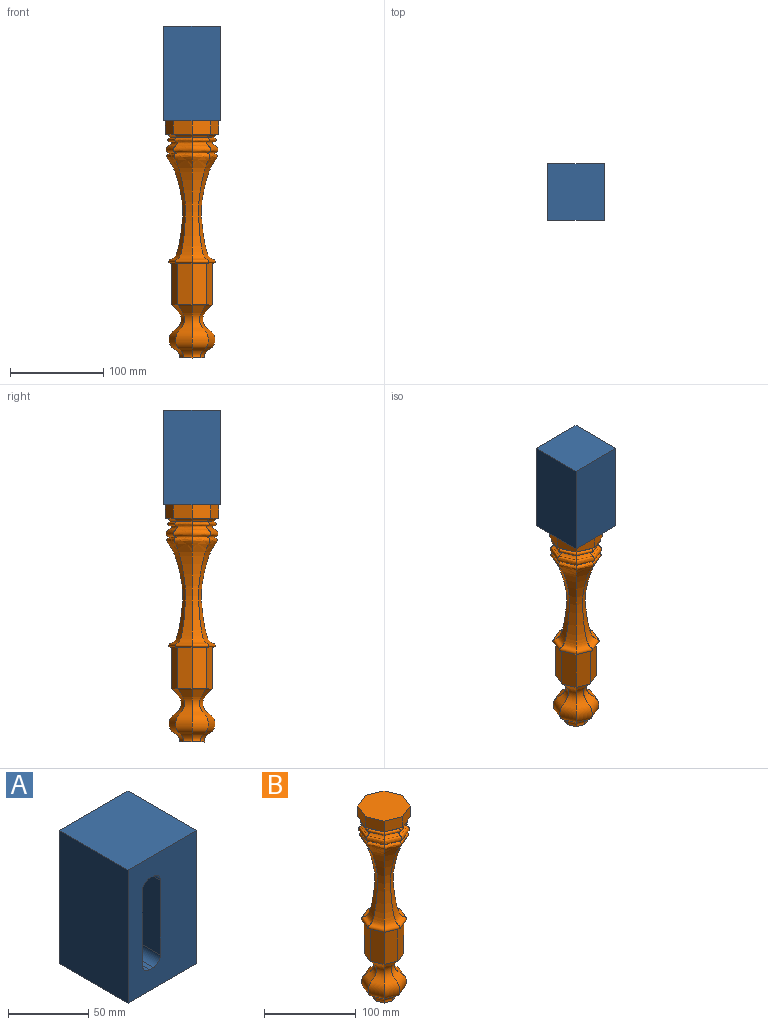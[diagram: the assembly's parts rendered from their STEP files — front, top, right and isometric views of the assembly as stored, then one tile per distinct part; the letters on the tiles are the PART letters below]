
ASSEMBLY  parts=2 mates=1
PART A: 24 faces, bbox 60.3x60.3x101.6 mm
  f0: plane 101.6x60.33mm, normal (1,0,0), area 5054.8mm2, adj f1,f3,f4,f5,f11,f12,f13,f14
  f1: plane 101.6x60.33mm, normal (0,1,0), area 6129mm2, adj f0,f2,f4,f5
  f2: plane 101.6x60.33mm, normal (-1,0,0), area 6129mm2, adj f1,f3,f4,f5
  f3: plane 101.6x60.33mm, normal (0,-1,0), area 5054.8mm2, adj f0,f2,f4,f5,f6,f7,f8,f9
  f4: plane 60.33x60.33mm, normal (0,0,1), area 3639.1mm2, adj f0,f1,f2,f3
  f5: plane 60.33x60.33mm, normal (0,0,-1), area 3639.1mm2, adj f0,f1,f2,f3
  f6: plane 57.15x30.48mm, normal (1,0,0), area 1741.9mm2, adj f3,f10,f20,f23
  f7: plane 30.48x3.18mm, normal (0,0,1), area 96.8mm2, adj f3,f10,f20,f21
  f8: plane 57.15x30.48mm, normal (-1,0,0), area 1741.9mm2, adj f3,f10,f21,f22
  f9: plane 30.48x3.18mm, normal (0,0,-1), area 96.8mm2, adj f3,f10,f22,f23
  f10: plane 69.85x15.88mm, normal (0,-1,0), area 1074.3mm2, adj f6,f7,f8,f9,f20,f21,f22,f23
  f11: plane 30.48x3.18mm, normal (0,0,1), area 96.8mm2, adj f0,f15,f16,f19
  f12: plane 57.15x30.48mm, normal (0,-1,0), area 1741.9mm2, adj f0,f15,f16,f17
  f13: plane 30.48x3.18mm, normal (0,0,-1), area 96.8mm2, adj f0,f15,f17,f18
  f14: plane 57.15x30.48mm, normal (0,1,0), area 1741.9mm2, adj f0,f15,f18,f19
  f15: plane 69.85x15.88mm, normal (1,0,0), area 1074.3mm2, adj f11,f12,f13,f14,f16,f17,f18,f19
  f16: cylinder r=6.35mm len=30.48mm, axis (-1,0,0), area 304mm2, adj f0,f11,f12,f15
  f17: cylinder r=6.35mm len=30.48mm, axis (1,0,0), area 304mm2, adj f0,f12,f13,f15
  f18: cylinder r=6.35mm len=30.48mm, axis (-1,0,0), area 304mm2, adj f0,f13,f14,f15
  f19: cylinder r=6.35mm len=30.48mm, axis (1,0,0), area 304mm2, adj f0,f11,f14,f15
  f20: cylinder r=6.35mm len=30.48mm, axis (0,1,0), area 304mm2, adj f3,f6,f7,f10
  f21: cylinder r=6.35mm len=30.48mm, axis (0,-1,0), area 304mm2, adj f3,f7,f8,f10
  f22: cylinder r=6.35mm len=30.48mm, axis (0,1,0), area 304mm2, adj f3,f8,f9,f10
  f23: cylinder r=6.35mm len=30.48mm, axis (0,-1,0), area 304mm2, adj f3,f6,f9,f10
PART B: 51 faces, bbox 56.8x56.8x254 mm
  f0: plane 20.1x14.35mm, normal (-0.38,0.92,0), area 312.2mm2, adj f1,f6,f7,f43
  f1: bspline ~20.1x12.02mm, area 129.9mm2, adj f0,f2,f8,f44
  f2: bspline ~134.07x20.71mm, area 1999.9mm2, adj f1,f3,f9,f45
  f3: plane 44.45x15.19mm, normal (-0.38,0.92,0), area 730.9mm2, adj f2,f4,f10,f46
  f4: bspline ~57.19x17.37mm, area 919.8mm2, adj f3,f5,f11,f47
  f5: plane 13.49x9.54mm, normal (0.01,-0.02,-1), area 64.4mm2, adj f4,f12,f48
  f6: plane 56.84x56.84mm, normal (0,0,1), area 2284.9mm2, adj f0,f7,f13,f19,f25,f31,f37,f43
  f7: plane 20.1x14.35mm, normal (-0.92,0.38,0), area 312.2mm2, adj f0,f6,f8,f13
  f8: bspline ~20.1x12.02mm, area 129.9mm2, adj f1,f7,f9,f14
  f9: bspline ~134.07x20.71mm, area 1999.9mm2, adj f2,f8,f10,f15
  f10: plane 44.45x15.19mm, normal (-0.92,0.38,0), area 730.9mm2, adj f3,f9,f11,f16
  f11: bspline ~57.19x17.37mm, area 919.8mm2, adj f4,f10,f12,f17
  f12: plane 13.49x9.54mm, normal (0.02,-0.01,-1), area 64.4mm2, adj f5,f11,f18
  f13: plane 20.1x14.35mm, normal (-0.92,-0.38,0), area 312.2mm2, adj f6,f7,f14,f19
  f14: bspline ~20.1x12.02mm, area 129.9mm2, adj f8,f13,f15,f20
  f15: bspline ~134.07x20.71mm, area 1999.9mm2, adj f9,f14,f16,f21
  f16: plane 44.45x15.19mm, normal (-0.92,-0.38,0), area 730.9mm2, adj f10,f15,f17,f22
  f17: bspline ~57.19x17.37mm, area 919.8mm2, adj f11,f16,f18,f23
  f18: plane 13.49x9.54mm, normal (0.02,0.01,-1), area 64.4mm2, adj f12,f17,f24
  f19: plane 20.1x14.35mm, normal (-0.38,-0.92,0), area 312.2mm2, adj f6,f13,f20,f25
  f20: bspline ~20.1x12.02mm, area 129.9mm2, adj f14,f19,f21,f26
  f21: bspline ~134.07x20.71mm, area 1999.9mm2, adj f15,f20,f22,f27
  f22: plane 44.45x15.19mm, normal (-0.38,-0.92,0), area 730.9mm2, adj f16,f21,f23,f28
  f23: bspline ~57.19x17.37mm, area 919.8mm2, adj f17,f22,f24,f29
  f24: plane 13.49x9.54mm, normal (0.01,0.02,-1), area 64.4mm2, adj f18,f23,f30
  f25: plane 20.1x14.35mm, normal (0.38,-0.92,0), area 312.2mm2, adj f6,f19,f26,f31
  f26: bspline ~20.1x12.02mm, area 129.9mm2, adj f20,f25,f27,f32
  f27: bspline ~134.07x20.71mm, area 1999.9mm2, adj f21,f26,f28,f33
  f28: plane 44.45x15.19mm, normal (0.38,-0.92,0), area 730.9mm2, adj f22,f27,f29,f34
  f29: bspline ~57.19x17.37mm, area 919.8mm2, adj f23,f28,f30,f35
  f30: plane 13.49x9.54mm, normal (-0.01,0.02,-1), area 64.4mm2, adj f24,f29,f36
  f31: plane 20.1x14.35mm, normal (0.92,-0.38,0), area 312.2mm2, adj f6,f25,f32,f37
  f32: bspline ~20.1x12.02mm, area 129.9mm2, adj f26,f31,f33,f38
  f33: bspline ~134.07x20.71mm, area 1999.9mm2, adj f27,f32,f34,f39
  f34: plane 44.45x15.19mm, normal (0.92,-0.38,0), area 730.9mm2, adj f28,f33,f35,f40
  f35: bspline ~57.19x17.37mm, area 919.8mm2, adj f29,f34,f36,f41
  f36: plane 13.49x9.54mm, normal (-0.02,0.01,-1), area 64.4mm2, adj f30,f35,f42
  f37: plane 20.1x14.35mm, normal (0.92,0.38,0), area 312.2mm2, adj f6,f31,f38,f43
  f38: bspline ~20.1x12.02mm, area 129.9mm2, adj f32,f37,f39,f44
  f39: bspline ~134.07x20.71mm, area 1999.9mm2, adj f33,f38,f40,f45
  f40: plane 44.45x15.19mm, normal (0.92,0.38,0), area 662.4mm2, adj f34,f39,f41,f46,f49
  f41: bspline ~57.19x17.37mm, area 919.8mm2, adj f35,f40,f42,f47
  f42: plane 13.49x9.54mm, normal (-0.02,-0.01,-1), area 64.4mm2, adj f36,f41,f48
  f43: plane 20.1x14.35mm, normal (0.38,0.92,0), area 312.2mm2, adj f0,f6,f37,f44
  f44: bspline ~20.1x12.02mm, area 129.9mm2, adj f1,f38,f43,f45
  f45: bspline ~134.07x20.71mm, area 1999.9mm2, adj f2,f39,f44,f46
  f46: plane 44.45x15.19mm, normal (0.38,0.92,0), area 662.4mm2, adj f3,f40,f45,f47,f49
  f47: bspline ~57.19x17.37mm, area 919.8mm2, adj f4,f41,f46,f48
  f48: plane 13.49x9.54mm, normal (-0.01,-0.02,-1), area 64.4mm2, adj f5,f42,f47
  f49: cylinder r=6.35mm len=22.45mm, axis (0.71,0.71,0), area 693.3mm2, adj f40,f46,f50
  f50: plane 12.7x8.98mm, normal (0.71,0.71,0), area 126.7mm2, adj f49
PLACE A rot(axis=(0,0,1),90deg) t=(-74.32,-89.54,-87.49)mm
PLACE B t=(-74.32,-89.54,-341.17)mm
MATE fastened A.f5 <-> B.f6  axis (0,0,-1) through (-74.32,-89.54,-87.49)mm
